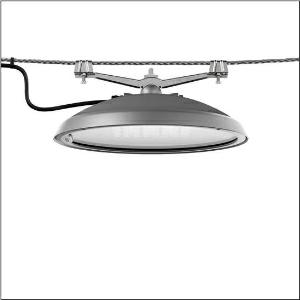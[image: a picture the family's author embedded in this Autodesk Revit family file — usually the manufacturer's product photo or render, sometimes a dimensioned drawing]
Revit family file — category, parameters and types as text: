
# Revit family: dl_50_iq_mini___st0_8s_5xa248v31f08ge_968e
name_source: partatom
category: Lighting Fixtures
units: mm (PartAtom-declared; Revit-internal decimal feet)

## family parameters
Cut with Voids When Loaded = No
Host = Face
Light Source = No
Part Type = Normal
Room Calculation Point = No
Round Connector Dimension = Use Diameter
Shared = No

## types (1)
- --- (1 x LED, 5190 lm, 32.7 W, 3000K)
    Apparent Load = 33 VA
    CIE Flux Codes = 38 75 97 100 100
    Color Rendering = 70
    Color Temperature = 3000K
    Default Elevation = 1800 mm
    Description = DL 50 iQ mini, catenary luminaire, primary light control with lens, of PMMA, primary optical cover: cover, of toughened safety glass, transparent, light distribution: ST0.8s, light emission: direct distribution, primary light characteristic: symmetric, installation type: suspended mounting, LED, High Power LED, rated luminous flux: 5.190lm, luminous efficacy: 159lm/W, light colour: 730, colour temperature: 3000K, control gear: iQ Street-Remote, control: optimised constant luminous flux control (CLO 2.0), Desk-Remote (wireless, voltage-free reading and setting of iQ features in the workshop via application-optimized NFC function/RFID function), Light-Fading, Smart-Wire, Night-Set, Lumen-Switch, Temp-Guard, Auto-Match, Street-Remote, mains connection: 230..240V, AC, 50/60Hz, start of lifetime: 33W, end of service life: 34W, reduction: 16W, luminaire housing, of diecast aluminium, powder-coated, SITECO metallic grey (DB 702S), diameter: 500mm, height: 115mm, mounting height: 4..12m, protection rating (complete): IP66, insulation class (complete): insulation class II (safety insulation), certification: CE, ENEC, ENEC+, VDE, impact resistance: IK08, permissible operating ambient temperature for outdoor applications: -25..+40°C, standard-compliant lighting for roads and squares, packaging unit: 1 piece

Light Distribution: ST0.8s
    Height = 124 mm  [stored 0.406824 ft]
    Lamp = 1 x LED
    Lamp Light Flux = 5190 lm
    Lamp Power = 32.7 W
    Lamp count = 1
    Length = 500 mm
    Luminous efficacy = 159 lm/W
    Manufacturer = Siteco
    ModVariant = No
    Model = 5XA248V31F08GE
    Number of Poles = 1
    OnlyDefault = Yes
    Power Factor = 1
    Product Name = DL 50 iQ mini | ST0.8s
    Product group = catenary luminaire
    ProductGroupID = 6300
    Protection Class = Protection class II
    Protection Degree = IP 66
    RLX_Detail_Level = 1
    RLX_Emergency_Light_Flux = 0 lm
    RLX_Emergency_Type = 0
    RLX_Emergency_Type_DB = No
    RlxData = <blob elided: 123661 chars, md5=5dd226ae>
    Socket = socket
    Standby Power = 0 W
    System Light Flux = 5190 lm
    System Power = 33 W
    Type Comments = factory setting: luminous flux: 100 % | dim-lin: 254 | 340 mA
    Type Image = l_1242791.jpg
    URL = http://relux.com
    VarID = @adj_142185
    Voltage = 0 V
    Weight = 0.00 kg
    Width = 0 mm  [stored 0 ft]

note: [stored X ft] marks values corroborated as IEEE doubles in the binary element streams (Revit-internal decimal feet)

## geometry (parser evidence)
native form markers: Blend x4, Sweep x13
no freeform markers — native parametric forms only
